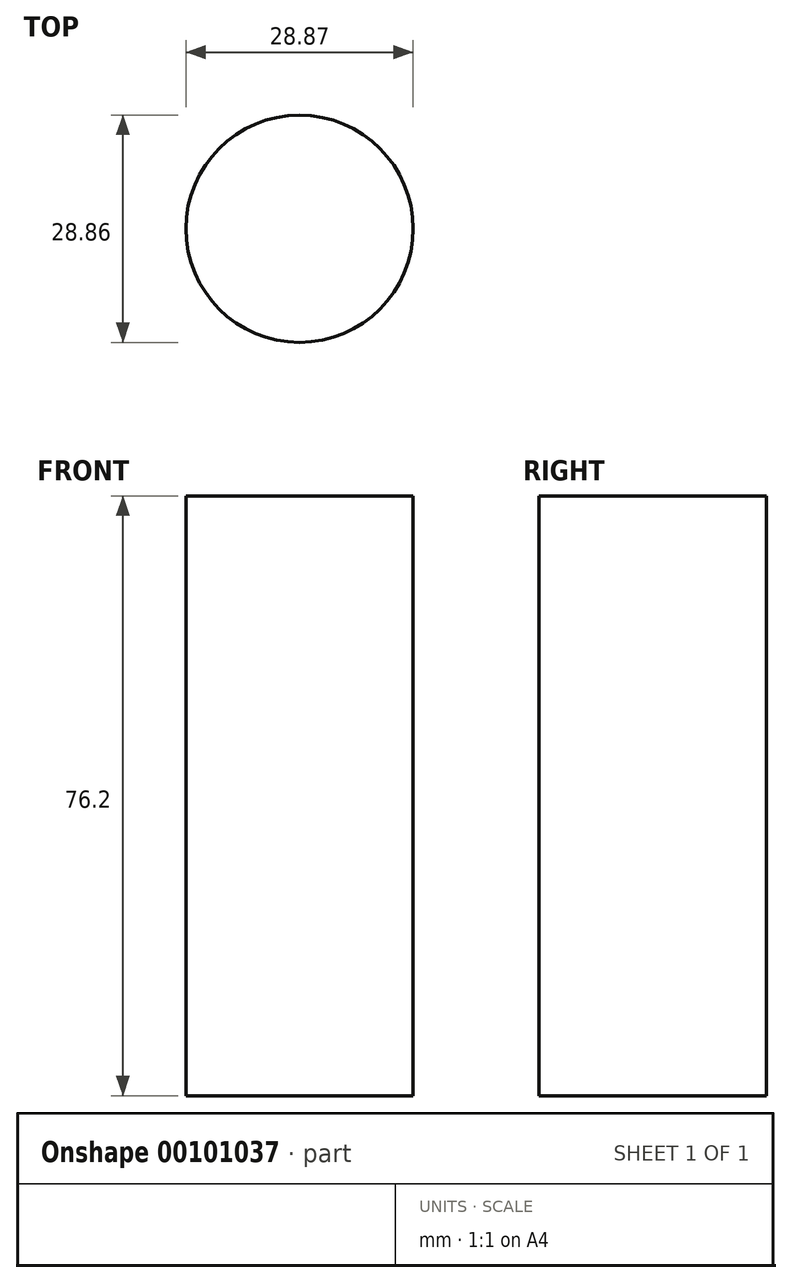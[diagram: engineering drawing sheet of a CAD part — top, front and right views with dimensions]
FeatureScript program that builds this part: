
annotation { "Feature Type Name" : "Feature", "Feature Type Description" : "" }
export const myFeature = defineFeature(function(context is Context, id is Id, definition is map)
    precondition{}
    {
        {
            var Q0;
            Q0=qCreatedBy(makeId("Top.planeOp"),FACE);
            var sketch = newSketch(context, id + "F0", { "sketchPlane" : qUnion([Q0])});
            skCircle(sketch, "E0", {"center": v(-39.21, -37.16) * mm, "radius": 14.43 * mm});
            skSolve(sketch);
        }
        {
            var Q0;
            Q0=sQuery(id+"F0.wireOp",EDGE,"E0");
            extrude(context, id + "F1", {"bodyType" : ToolBodyType.SURFACE, "surfaceEntities" : qUnion([Q0]), "depth" : 76.2 * mm});
        }
    });
